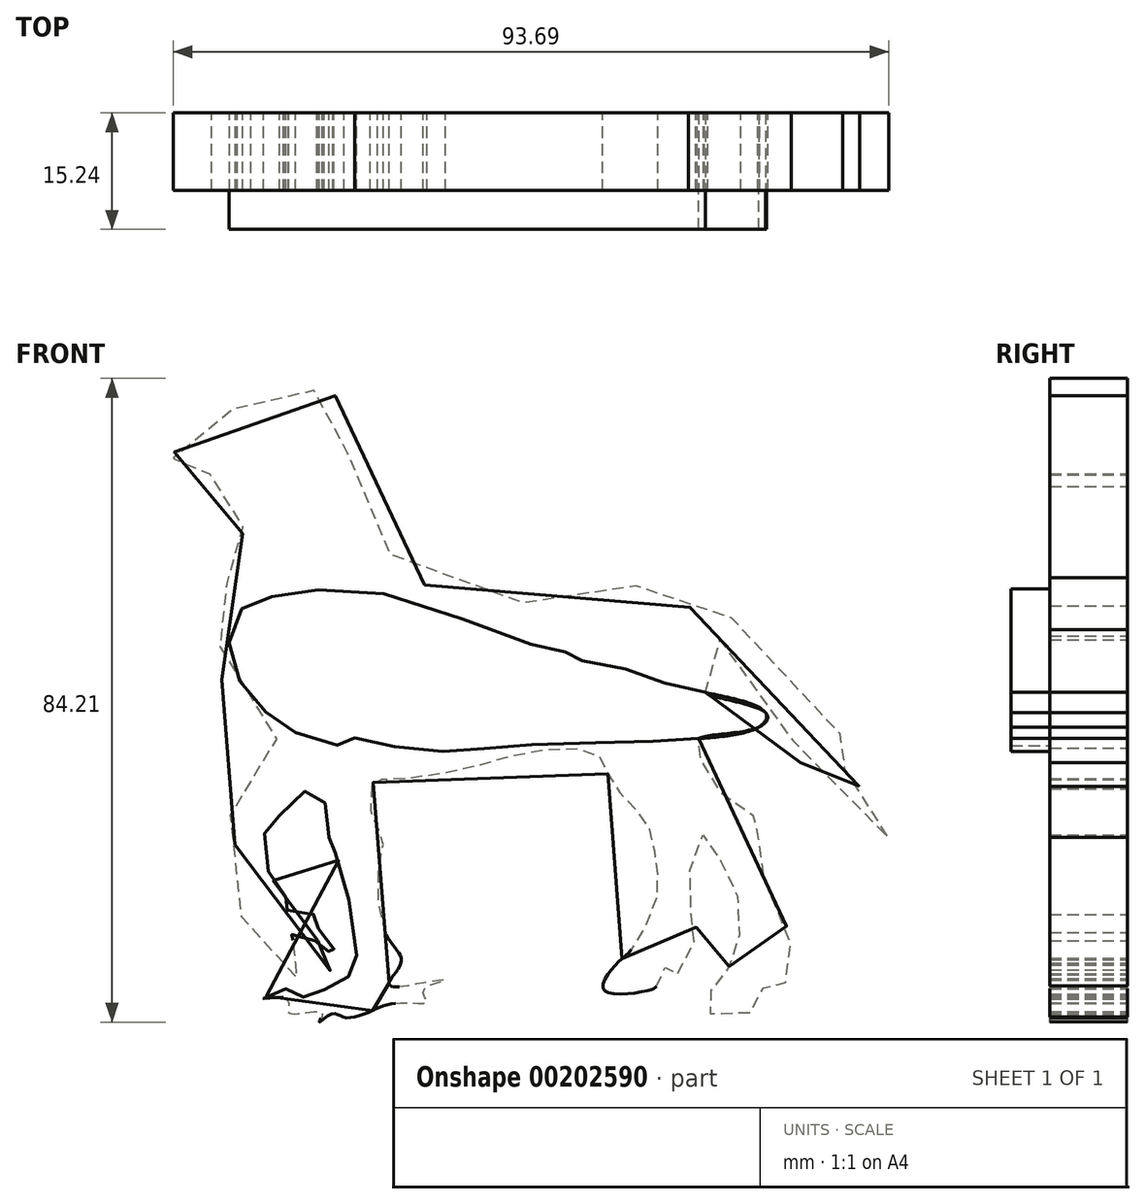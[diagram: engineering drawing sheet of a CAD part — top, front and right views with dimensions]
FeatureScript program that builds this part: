
annotation { "Feature Type Name" : "Feature", "Feature Type Description" : "" }
export const myFeature = defineFeature(function(context is Context, id is Id, definition is map)
    precondition{}
    {
        {
            var Q0;
            Q0=qCreatedBy(makeId("Front.planeOp"),FACE);
            var sketch = newSketch(context, id + "F0", { "sketchPlane" : qUnion([Q0])});
            skFitSpline(sketch, "E0", {"points": [v(-58.55, 34.58) * mm, v(-60.67, 33.85) * mm, v(-63.13, 31.12) * mm, v(-62.6, 26.94) * mm, v(-62.2, 28.13) * mm, v(-59.88, 28.47) * mm, v(-58.41, 28.6) * mm, v(-54.83, 27.87) * mm, v(-53.03, 25.6) * mm, v(-54.1, 21.89) * mm, v(-54.16, 19.76) * mm, v(-55.02, 18.3) * mm, v(-54.9, 15.44) * mm, v(-56.22, 14.18) * mm, v(-57.55, 8.92) * mm, v(-58.15, 6.86) * mm, v(-57.42, 7.4) * mm, v(-56.86, 1.88) * mm, v(-53.67, -2.64) * mm, v(-49.28, -7.23) * mm, v(-52.74, -12.28) * mm, v(-55.33, -14.6) * mm, v(-55.73, -18) * mm, v(-55, -20.52) * mm, v(-54.37, -29.19) * mm, v(-52.95, -30.07) * mm, v(-50.38, -34.78) * mm, v(-47.63, -37.17) * mm, v(-42.84, -36.9) * mm, v(-42.3, -36.29) * mm, v(-45.06, -36.9) * mm, v(-47.1, -35.13) * mm, v(-43.46, -35.4) * mm, v(-46.03, -34.42) * mm, v(-47.1, -32.91) * mm, v(-48.6, -31.4) * mm, v(-45.68, -32.38) * mm, v(-44.44, -32.47) * mm, v(-43.1, -33.18) * mm, v(-42.66, -34.78) * mm, v(-42.22, -32.91) * mm, v(-44.35, -30.6) * mm, v(-44.35, -29.19) * mm, v(-47.19, -29.01) * mm, v(-48.78, -27.68) * mm, v(-48.43, -26.97) * mm, v(-50.65, -23.69) * mm, v(-50.91, -17.57) * mm, v(-48.96, -15.88) * mm, v(-44.97, -12.6) * mm, v(-42.84, -16.59) * mm, v(-42.75, -20.14) * mm, v(-41.95, -21.11) * mm, v(-39.2, -34.24) * mm, v(-39.91, -36.9) * mm, v(-42.93, -38.6) * mm, v(-45.5, -39.83) * mm, v(-47.28, -39.48) * mm, v(-48.96, -38.77) * mm, v(-51.36, -40.1) * mm, v(-49.58, -39.75) * mm, v(-48.07, -40.72) * mm, v(-47.99, -41.96) * mm, v(-43.73, -41.96) * mm, v(-44.08, -43.12) * mm, v(-42.4, -42.05) * mm, v(-40.89, -42.5) * mm, v(-37.7, -41.87) * mm, v(-35.03, -40.81) * mm, v(-31.66, -40.63) * mm, v(-29.98, -40.46) * mm, v(-30.42, -38.95) * mm, v(-27.58, -37.62) * mm, v(-31.3, -38.15) * mm, v(-33.26, -38.5) * mm, v(-34.94, -38.15) * mm, v(-33.35, -35.3) * mm, v(-35.12, -32.03) * mm, v(-36.27, -22.71) * mm, v(-35.74, -18.9) * mm, v(-37.07, -16.68) * mm, v(-36.9, -11.53) * mm, v(-35.74, -11.35) * mm, v(-25.72, -10.11) * mm, v(-16.67, -7.8) * mm, v(-7.97, -7.9) * mm, v(-6.38, -10.47) * mm, v(-3.98, -13.93) * mm, v(-1.05, -17.48) * mm, v(0, -22.44) * mm, v(0, -27.15) * mm, v(-3.36, -33.8) * mm, v(-4.96, -35.3) * mm, v(-6.82, -38.95) * mm, v(-0.79, -38.95) * mm, v(0, -38.5) * mm, v(0.9, -36.9) * mm, v(1.52, -35.66) * mm, v(2.85, -36.82) * mm, v(5.25, -30.87) * mm, v(4.36, -28.39) * mm, v(5.87, -18.72) * mm, v(8.17, -21.47) * mm, v(11.01, -28.21) * mm, v(9.95, -35.13) * mm, v(7.82, -38.24) * mm, v(6.4, -41.52) * mm, v(12.7, -41.6) * mm, v(14.2, -38.5) * mm, v(16.82, -38.1) * mm, v(17.22, -30.93) * mm, v(15.53, -28.24) * mm, v(13.34, -18.58) * mm, v(13.44, -16.79) * mm, v(8.66, -13.3) * mm, v(5.37, -7.42) * mm, v(5.57, -6.03) * mm, v(13.44, -4.54) * mm, v(14.33, -2.64) * mm, v(6.47, 0) * mm, v(6.76, 1.74) * mm, v(5.47, 7.91) * mm, v(7.66, 7.51) * mm, v(13.44, 0) * mm, v(17.32, -4.93) * mm, v(22.9, -15.79) * mm, v(30.47, -18.98) * mm, v(26.88, -16.59) * mm, v(24.5, -9.22) * mm, v(25.78, -12.1) * mm, v(26.68, -12.1) * mm, v(26.08, -11.4) * mm, v(24.3, -6.73) * mm, v(21.4, 2.24) * mm, v(6.96, 10.8) * mm, v(4.77, 11.1) * mm, v(0, 12.9) * mm, v(-7.18, 14.98) * mm, v(-11.86, 13.39) * mm, v(-24.6, 11.6) * mm, v(-33.97, 17.17) * mm, v(-36.06, 20.26) * mm, v(-37.96, 25.75) * mm, v(-40.78, 34.77) * mm, v(-39.56, 38.62) * mm, v(-44.07, 39.1) * mm, v(-46.51, 41.07) * mm, v(-50.46, 38.81) * mm, v(-55.82, 36.84) * mm, v(-58.55, 34.58) * mm]});
            skFitSpline(sketch, "E1", {"points": [v(-49.4, 12.64) * mm, v(-53.67, 11.47) * mm, v(-55.84, 7.12) * mm, v(-54.34, 1.25) * mm, v(-50.15, -3.35) * mm, v(-45.54, -5.95) * mm, v(-40.02, -6.79) * mm, v(-39.6, -6.03) * mm, v(-33.65, -7.2) * mm, v(-25.2, -7.62) * mm, v(-18.16, -6.95) * mm, v(-3.09, -6.45) * mm, v(5.57, -6.03) * mm, v(13.44, -4.54) * mm, v(14.33, -2.64) * mm, v(6.47, 0) * mm, v(0, 1.62) * mm, v(-7.02, 3.83) * mm, v(-11.54, 4.63) * mm, v(-11.8, 5.25) * mm, v(-15.45, 6.05) * mm, v(-36.87, 13.17) * mm, v(-49.4, 12.64) * mm]});
            skFitSpline(sketch, "E2", {"points": [v(-47.13, 0) * mm, v(-44.24, 0) * mm, v(-45.23, 2.51) * mm, v(-42.25, 2.51) * mm, v(-42.44, 3.7) * mm, v(-38.76, 1.82) * mm, v(-38.96, 2.71) * mm, v(-35.37, 1.22) * mm, v(-36.37, 3.51) * mm, v(-35.08, 4.6) * mm, v(-36.77, 6.2) * mm, v(-33.38, 5.4) * mm, v(-34.58, 7) * mm, v(-32.59, 7.7) * mm, v(-33.38, 8.59) * mm, v(-38.66, 10.88) * mm, v(-39.26, 9.98) * mm, v(-39.16, 8.79) * mm, v(-42.34, 8.69) * mm, v(-41.25, 6.3) * mm, v(-43.14, 6.1) * mm, v(-45.63, 5) * mm, v(-45.83, 3.21) * mm, v(-48.32, 2.42) * mm, v(-47.13, 0) * mm]});
            skSolve(sketch);
        }
        {
            var Q0;
            Q0 = qSketchRegion(id + "F0", true);
            var Q1;
            Q1=makeQuery(id+"F0.imprint","IMPRINT",FACE,{"disambiguationData":[TD([[makeQuery(id+"F0.imprint","IMPRINT",EDGE,{"derivedFrom":sQuery(id+"F0.wireOp",EDGE,"E2")}),1.0]])]});
            extrude(context, id + "F1", {"entities" : qUnion([Q0, Q1]), "oppositeDirection" : true, "depth" : 10.16 * mm});
        }
        {
            var Q0;
            Q0=makeQuery(id+"F0.imprint","IMPRINT",FACE,{"disambiguationData":[TD([[makeQuery(id+"F0.imprint","IMPRINT",EDGE,{"derivedFrom":sQuery(id+"F0.wireOp",EDGE,"E2")}),-1.0]])]});
            var Q1;
            Q1=makeQuery(id+"F0.imprint","IMPRINT",FACE,{"disambiguationData":[TD([[makeQuery(id+"F0.imprint","IMPRINT",EDGE,{"derivedFrom":sQuery(id+"F0.wireOp",EDGE,"E2")}),1.0]])]});
            extrude(context, id + "F2", {"entities" : qUnion([Q0, Q1]), "operationType" : NewBodyOperationType.ADD, "depth" : 5.08 * mm});
        }
        {
            var Q0;
            Q0=sQuery(id+"F0.wireOp",EDGE,"E2");
            extrude(context, id + "F3", {"bodyType" : ToolBodyType.SURFACE, "surfaceEntities" : qUnion([Q0]), "depth" : 10.16 * mm});
        }
    });
